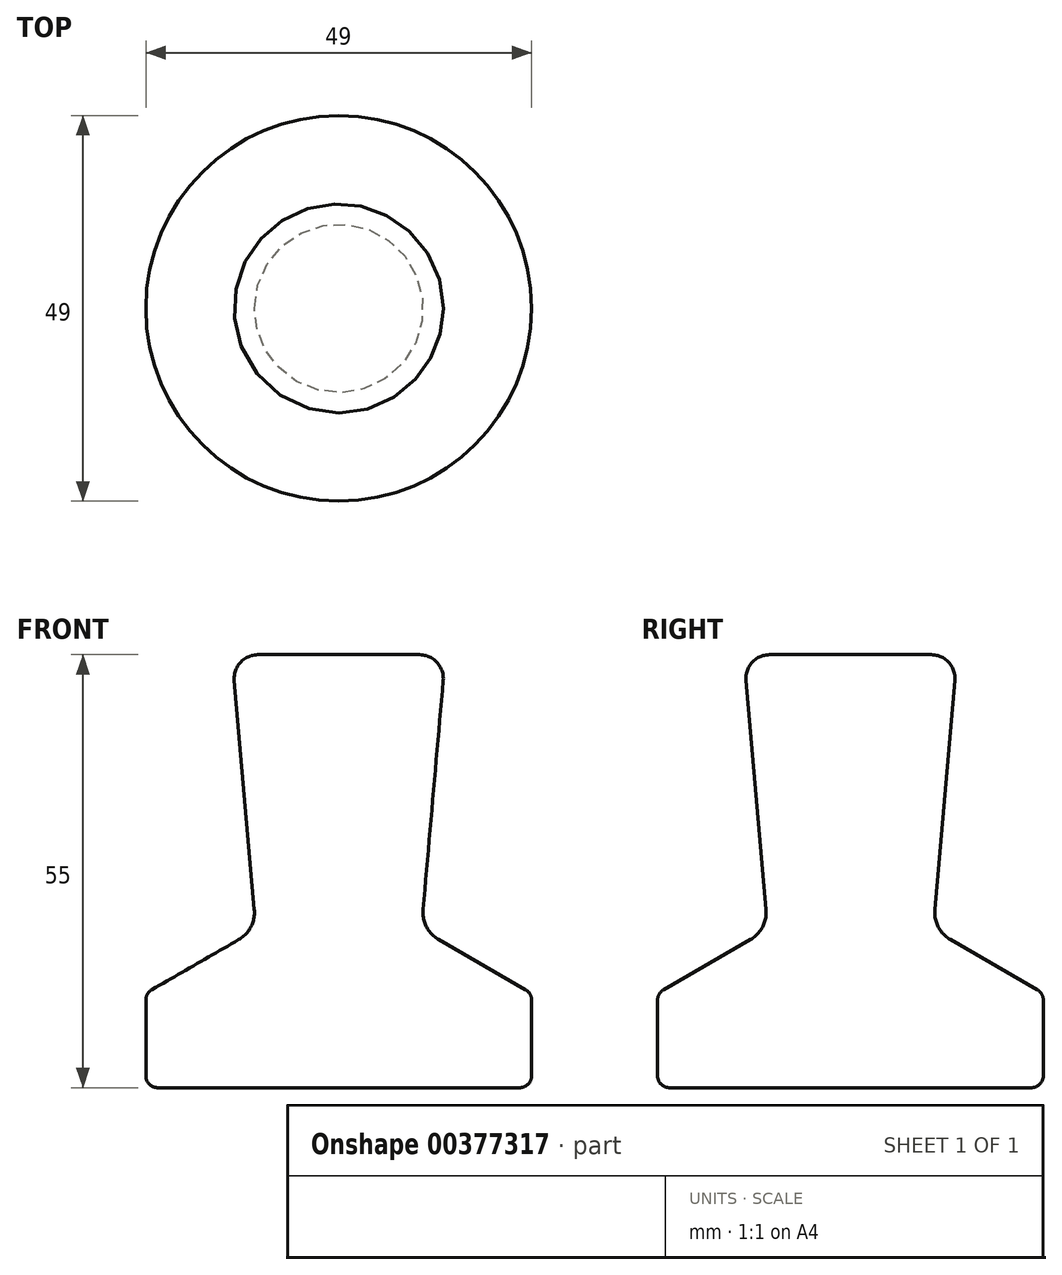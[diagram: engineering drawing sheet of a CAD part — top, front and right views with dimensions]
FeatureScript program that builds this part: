
annotation { "Feature Type Name" : "Feature", "Feature Type Description" : "" }
export const myFeature = defineFeature(function(context is Context, id is Id, definition is map)
    precondition{}
    {
        {
            var Q0;
            Q0=qCreatedBy(makeId("Front.planeOp"),FACE);
            var sketch = newSketch(context, id + "F0", { "sketchPlane" : qUnion([Q0])});
            skLineSegment(sketch, "E0", {"start": v(0, 0) * mm, "end": v(24.5, 0) * mm});
            skLineSegment(sketch, "E1", {"start": v(24.5, 0) * mm, "end": v(24.5, 12) * mm});
            skLineSegment(sketch, "E2", {"start": v(24.5, 12) * mm, "end": v(10.5, 20.08) * mm});
            skLineSegment(sketch, "E3", {"start": v(0, 0) * mm, "end": v(0, 55) * mm});
            skLineSegment(sketch, "E4", {"start": v(10.5, 20.08) * mm, "end": v(13.55, 55) * mm});
            skLineSegment(sketch, "E5", {"start": v(13.55, 55) * mm, "end": v(0, 55) * mm});
            skLineSegment(sketch, "E6", {"start": v(24.5, 12) * mm, "end": v(24.5, 20.08) * mm, "construction": true});
            skLineSegment(sketch, "E7", {"start": v(10.5, 20.08) * mm, "end": v(10.5, 55) * mm, "construction": true});
            skSolve(sketch);
        }
        {
            var Q0;
            Q0 = qSketchRegion(id + "F0", true);
            var Q1;
            Q1=sQuery(id+"F0.wireOp",EDGE,"E3");
            revolve(context, id + "F1", {"entities" : qUnion([Q0]), "axis" : qUnion([Q1]), "revolveType" : RevolveType.FULL});
        }
        {
            var Q0;
            Q0=makeQuery(id+"F1.opRevolve","SWEPT_EDGE",EDGE,{"disambiguationData":[OSD([sQuery(id+"F0.wireOp",EDGE,"E0"),sQuery(id+"F0.wireOp",EDGE,"E1")])]});
            var Q1;
            Q1=makeQuery(id+"F1.opRevolve","SWEPT_EDGE",EDGE,{"disambiguationData":[OSD([sQuery(id+"F0.wireOp",EDGE,"E1"),sQuery(id+"F0.wireOp",EDGE,"E2")])]});
            fillet(context, id + "F2", {"entities" : qUnion([Q0, Q1]), "radius" : 1.5 * mm, "tangentPropagation" : true, "allowEdgeOverflow" : false});
        }
        {
            var Q0;
            Q0=makeQuery(id+"F1.opRevolve","SWEPT_EDGE",EDGE,{"disambiguationData":[OSD([sQuery(id+"F0.wireOp",EDGE,"E2"),sQuery(id+"F0.wireOp",EDGE,"E4")])]});
            fillet(context, id + "F3", {"entities" : qUnion([Q0]), "radius" : 4 * mm, "tangentPropagation" : true, "allowEdgeOverflow" : false});
        }
        {
            var Q0;
            Q0=makeQuery(id+"F1.opRevolve","SWEPT_EDGE",EDGE,{"disambiguationData":[OSD([sQuery(id+"F0.wireOp",EDGE,"E4"),sQuery(id+"F0.wireOp",EDGE,"E5")])]});
            fillet(context, id + "F4", {"entities" : qUnion([Q0]), "radius" : 3 * mm, "tangentPropagation" : true, "allowEdgeOverflow" : false});
        }
    });
